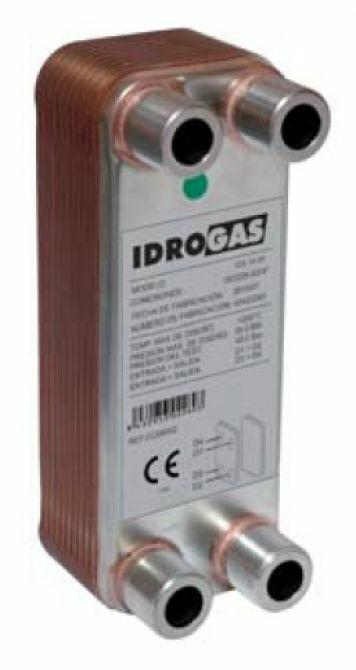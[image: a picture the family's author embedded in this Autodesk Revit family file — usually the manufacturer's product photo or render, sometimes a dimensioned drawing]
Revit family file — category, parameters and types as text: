
# Revit family: IDS110-30_CC08053
name_source: partatom
category: Aparatos eléctricos
revit_build: Autodesk Revit 2016 (Build: 20150220_1215(x64)
units: mm (PartAtom-declared; Revit-internal decimal feet)

## family parameters
Compartido = No
Corte con vacíos al cargar = No
Cota de conector redondo = Diámetro de uso
Mantener orientación de anotación = No
Número OmniClass = 23.80.00.00
Punto de cálculo de habitación = No
Se basa en plano de trabajo = No
Siempre vertical = Sí
Tipo de pieza = Caja de conexiones
Título OmniClass = Electric Power and Lighting

## types (1)
- IDS 110-30
    Caudal máx. = 34 m3/h
    Conexiones = 316L acero inox.
    Costo = 0 $
    Código de montaje = CC08053
    Descripción = INTERCAMBIADOR PLACAS TERMOSOLDADO
    Dimensiones = 616 x 191 x ~81,5 mm
    Fabricante = SALVADOR ESCODA
    Imagen de tipo = IDS-14.jpg
    Material soldadura = 99,99% cobre
    Modelo = IDS 110-30
    Peso = 17,8 Kg
    Placas = 316L acero inox.
    Placas cubierta = 304 acero inox.
    Presión trabajo = 0-30/45 bar
    Temperatura máx. trabajo = 225 ºC
    URL = www.salvadorescoda.com
